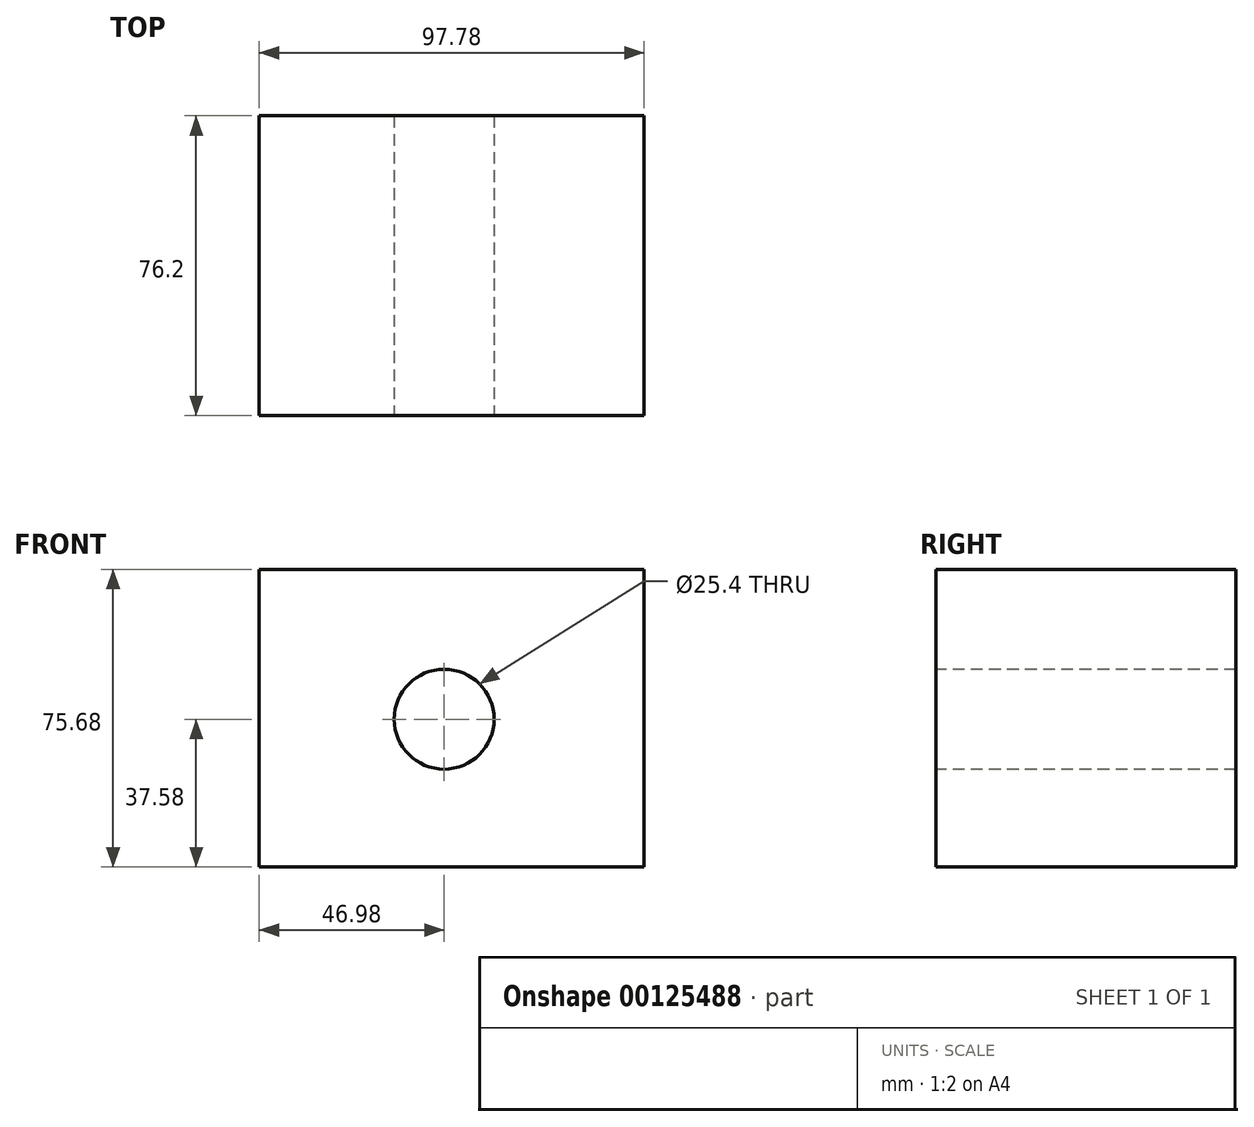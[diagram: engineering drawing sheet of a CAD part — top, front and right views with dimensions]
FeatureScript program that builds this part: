
annotation { "Feature Type Name" : "Feature", "Feature Type Description" : "" }
export const myFeature = defineFeature(function(context is Context, id is Id, definition is map)
    precondition{}
    {
        {
            var Q0;
            Q0=qCreatedBy(makeId("Front.planeOp"),FACE);
            var sketch = newSketch(context, id + "F0", { "sketchPlane" : qUnion([Q0])});
            skLineSegment(sketch, "E0.bottom", {"start": v(-46.98, 38.1) * mm, "end": v(50.8, 38.1) * mm});
            skLineSegment(sketch, "E0.top", {"start": v(-46.98, -37.58) * mm, "end": v(50.8, -37.58) * mm});
            skLineSegment(sketch, "E0.left", {"start": v(-46.98, 38.1) * mm, "end": v(-46.98, -37.58) * mm});
            skLineSegment(sketch, "E0.right", {"start": v(50.8, 38.1) * mm, "end": v(50.8, -37.58) * mm});
            skSolve(sketch);
        }
        {
            var Q0;
            Q0=makeQuery(id+"F0.imprint","IMPRINT",FACE,{"disambiguationData":[TD([[makeQuery(id+"F0.imprint","IMPRINT",EDGE,{"derivedFrom":sQuery(id+"F0.wireOp",EDGE,"E0.bottom")}),-1.0]])]});
            extrude(context, id + "F1", {"entities" : qUnion([Q0]), "endBound" : BoundingType.SYMMETRIC, "depth" : 76.2 * mm});
        }
        {
            var Q0;
            Q0=makeQuery(id+"F1.opExtrude","CAP_FACE",FACE,{"disambiguationData":[OSD([sQuery(id+"F0.wireOp",EDGE,"E0.bottom"),sQuery(id+"F0.wireOp",EDGE,"E0.top"),sQuery(id+"F0.wireOp",EDGE,"E0.left"),sQuery(id+"F0.wireOp",EDGE,"E0.right")])],"isStart":false});
            var sketch = newSketch(context, id + "F2", { "sketchPlane" : qUnion([Q0])});
            skPoint(sketch, "E1", {"position": v(0, 0) * mm});
            skSolve(sketch);
        }
        {
            var Q0;
            Q0=sQuery(id+"F2.wireOp",VERTEX,"E1");
            var Q1;
            Q1=makeQuery(id+"F1.opExtrude","SWEPT_BODY",BODY,{"disambiguationData":[OSD([sQuery(id+"F0.wireOp",EDGE,"E0.bottom"),sQuery(id+"F0.wireOp",EDGE,"E0.top"),sQuery(id+"F0.wireOp",EDGE,"E0.left"),sQuery(id+"F0.wireOp",EDGE,"E0.right")])]});
            hole(context, id + "F3", {"style" : HoleStyle.SIMPLE, "endStyle" : HoleEndStyle.THROUGH, "holeDiameter" : 25.4 * mm, "locations" : qUnion([Q0]), "scope" : qUnion([Q1]), "isTappedThrough" : true});
        }
    });
